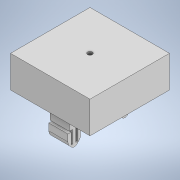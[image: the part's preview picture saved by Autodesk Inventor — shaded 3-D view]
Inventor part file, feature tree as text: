
AUTODESK INVENTOR PART (.ipt)
format: ipt  version: 2020 (Build 240168000, 168)  size: 251,392 bytes
history: native  units: mm
features: sketch x10, extrude x9, fillet x4, chamfer x3, hole x1
ambient origin geometry x8: Origin, YZ Plane, XZ Plane, XY Plane, X Axis, Y Axis, Z Axis, Center Point
bodies: Solid1 (feature_tree)
feature tree (27):
  extrude  "Extrusion1"  Depth=25.0mm
  extrude  "Extrusion2"  Depth=8.0mm
  extrude  "Extrusion3"  Depth=8.0mm
  extrude  "Extrusion4"  Depth=5.0mm TaperAngle=0.0deg
  extrude  "Extrusion5"  Depth=3.0mm
  extrude  "Extrusion6"  Depth=3.0mm
  extrude  "Extrusion7"  Depth=1.0mm
  extrude  "Extrusion8"  Depth=1.0mm
  extrude  "Extrusion9"  Depth=2.0mm
  chamfer  "Chamfer1"  Distance=2.0mm
  chamfer  "Chamfer2"  Distance=1.0mm
  fillet  "Fillet1"  Radius=4.5mm
  fillet  "Fillet2"  Radius=1.0mm
  chamfer  "Chamfer3"  Distance=4.5mm
  fillet  "Fillet3"  Radius=1.0mm
  fillet  "Fillet4"  Radius=4.5mm
  hole  "Hole1"  [1 undecoded]
  sketch  "Sketch1"  dims[d0=25.0mm d1=25.0mm]
  sketch  "Sketch2"  dims[d2=8.0mm d3=8.0mm]
  sketch  "Sketch4"  dims[d4=8.0mm d5=8.0mm]
  sketch  "Sketch5"  dims[d6=5.0mm d7=0.0mm d8=5.0mm d9=0.0mm]
  sketch  "Sketch6"  dims[d12=6.0mm d13=3.0mm]
  sketch  "Sketch7"  dims[d14=6.0mm d15=3.0mm]
  sketch  "Sketch8"  dims[d16=5.0mm d17=0.0mm d18=1.0mm]
  sketch  "Sketch9"  dims[d19=6.0mm d20=1.0mm]
  sketch  "Sketch10"  dims[d21=4.0mm d22=0.0mm d23=2.0mm]
  sketch  "Sketch11"  dims[d24=6.0mm d25=2.0mm d26=1.0mm d27=0.0mm d28=4.5mm d29=1.0mm d30=0.0mm d31=4.5mm d32=1.0mm d33=0.0mm d34=4.5mm d35=1.0mm d36=0.0mm d37=4.5mm d38=1.0mm d39=0.0mm d40=1.5mm d41=2.0mm d42=45.0deg d43=1.5mm d44=2.0mm d45=45.0deg d46=2.0mm d47=1.0mm d48=1.5mm d49=2.0mm d50=45.0deg d51=1.0mm d52=2.0mm d53=1.5mm d54=1.5mm d55=6.0mm d56=4.0mm d57=2.0mm d58=90.0deg d59=10.0mm d60=0.0mm]
note: 1 required parameter value undecoded (feature->parameter linkage not recoverable at this tier; creation-order binding heuristic only, values carry confidence <= 0.55)
